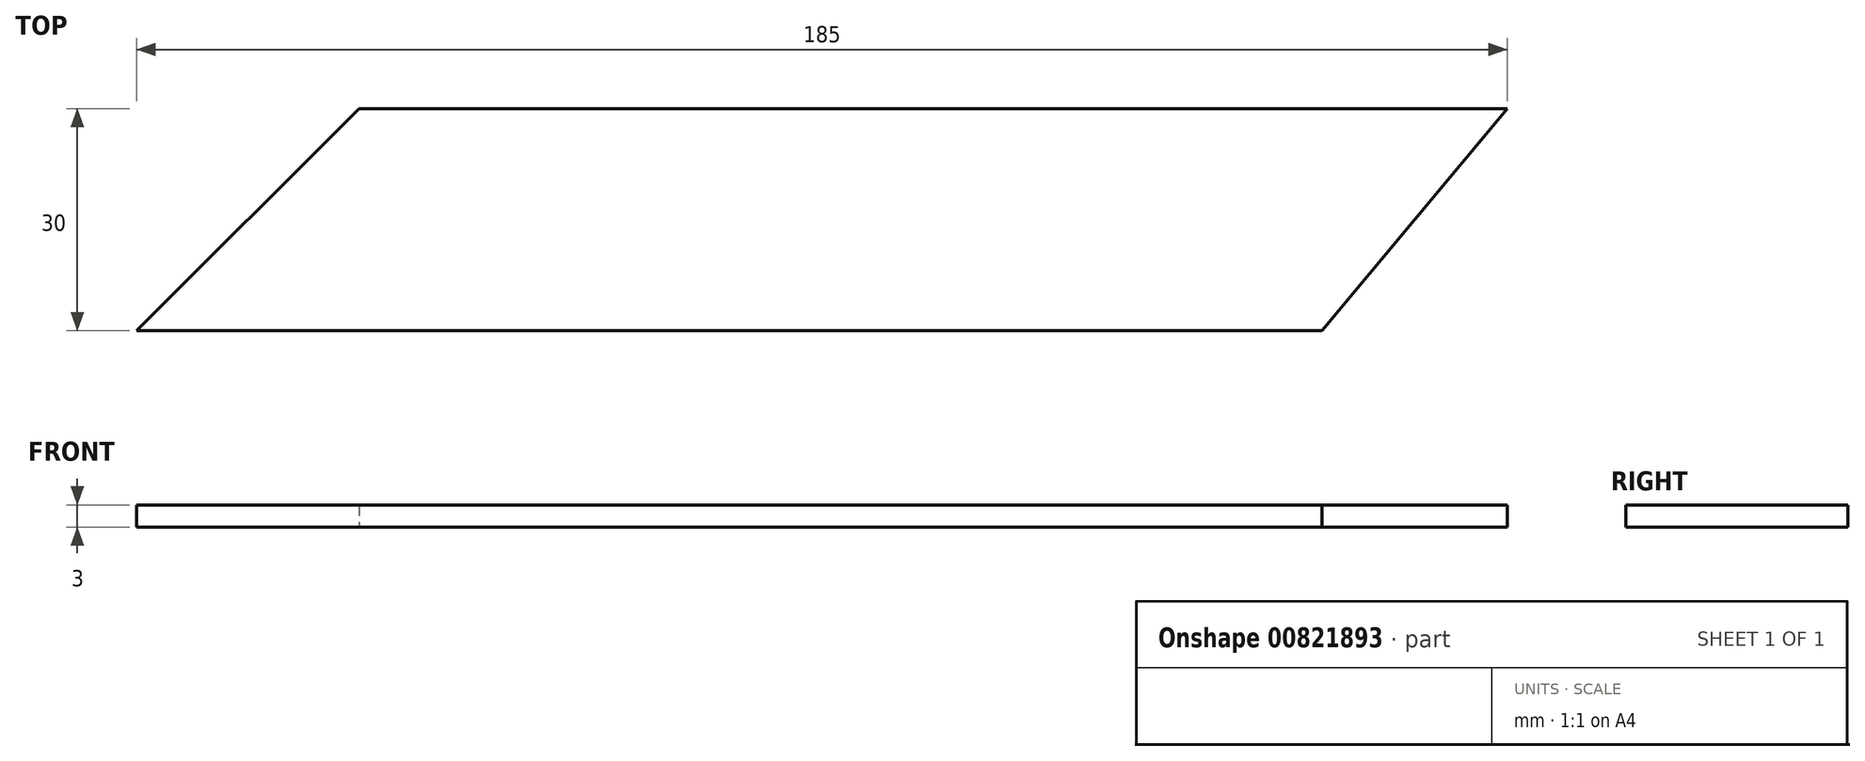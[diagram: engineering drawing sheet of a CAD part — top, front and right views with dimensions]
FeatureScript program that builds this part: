
annotation { "Feature Type Name" : "Feature", "Feature Type Description" : "" }
export const myFeature = defineFeature(function(context is Context, id is Id, definition is map)
    precondition{}
    {
        {
            var Q0;
            Q0=qCreatedBy(makeId("Top.planeOp"),FACE);
            var sketch = newSketch(context, id + "F0", { "sketchPlane" : qUnion([Q0])});
            skLineSegment(sketch, "E0", {"start": v(8.05, 0) * mm, "end": v(168.05, 0) * mm});
            skLineSegment(sketch, "E1", {"start": v(8.05, 0) * mm, "end": v(38.05, 30) * mm});
            skLineSegment(sketch, "E2", {"start": v(193.05, 30) * mm, "end": v(168.05, 0) * mm});
            skLineSegment(sketch, "E3", {"start": v(38.05, 30) * mm, "end": v(193.05, 30) * mm});
            skSolve(sketch);
        }
        {
            var Q0;
            Q0=makeQuery(id+"F0.imprint","IMPRINT",FACE,{"disambiguationData":[TD([[makeQuery(id+"F0.imprint","IMPRINT",EDGE,{"derivedFrom":sQuery(id+"F0.wireOp",EDGE,"E1")}),-1.0]])]});
            extrude(context, id + "F1", {"entities" : qUnion([Q0]), "depth" : 3 * mm, "offsetDistance" : 25.4 * mm});
        }
    });
